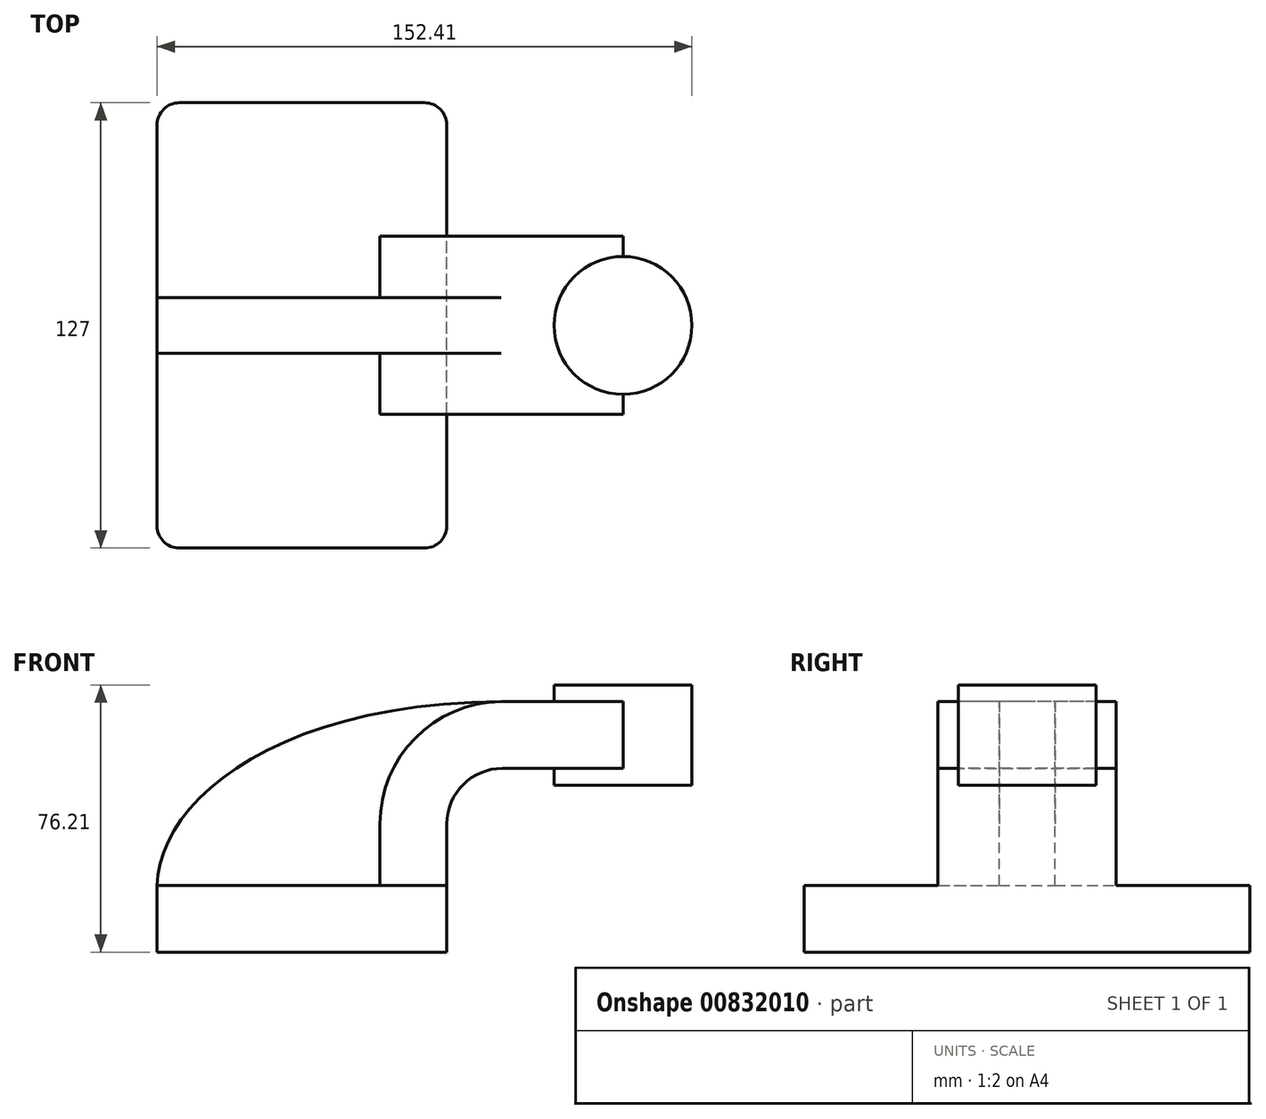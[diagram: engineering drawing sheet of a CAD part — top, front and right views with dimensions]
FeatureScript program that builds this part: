
annotation { "Feature Type Name" : "Feature", "Feature Type Description" : "" }
export const myFeature = defineFeature(function(context is Context, id is Id, definition is map)
    precondition{}
    {
        {
            var Q0;
            Q0=qCreatedBy(makeId("Front.planeOp"),FACE);
            var sketch = newSketch(context, id + "F0", { "sketchPlane" : qUnion([Q0])});
            skLineSegment(sketch, "E0.bottom", {"start": v(-41.28, 9.52) * mm, "end": v(41.27, 9.53) * mm});
            skLineSegment(sketch, "E0.top", {"start": v(-41.28, -9.52) * mm, "end": v(41.28, -9.52) * mm});
            skLineSegment(sketch, "E0.left", {"start": v(-41.28, 9.52) * mm, "end": v(-41.28, -9.53) * mm});
            skLineSegment(sketch, "E0.right", {"start": v(41.27, 9.53) * mm, "end": v(41.28, -9.52) * mm});
            skPoint(sketch, "E0.middle", {"position": v(0, 0) * mm});
            skLineSegment(sketch, "E1.bottom", {"start": v(111.13, 38.1) * mm, "end": v(60.32, 38.1) * mm});
            skLineSegment(sketch, "E1.top", {"start": v(111.12, 66.68) * mm, "end": v(60.32, 66.68) * mm});
            skLineSegment(sketch, "E1.left", {"start": v(111.12, 38.1) * mm, "end": v(111.12, 66.68) * mm});
            skLineSegment(sketch, "E1.right", {"start": v(60.32, 38.1) * mm, "end": v(60.32, 66.67) * mm});
            skPoint(sketch, "E1.middle", {"position": v(85.72, 52.39) * mm});
            skLineSegment(sketch, "E2", {"start": v(41.27, 9.53) * mm, "end": v(41.27, 27) * mm});
            skArc(sketch, "E3", {"start": v(41.27, 27) * mm, "mid": v(45.92, 38.23) * mm, "end": v(57.15, 42.88) * mm});
            skLineSegment(sketch, "E4", {"start": v(57.15, 42.88) * mm, "end": v(91.47, 42.88) * mm});
            skLineSegment(sketch, "E5.0", {"start": v(57.15, 61.93) * mm, "end": v(91.47, 61.93) * mm});
            skArc(sketch, "E5.1", {"start": v(22.22, 27) * mm, "mid": v(32.45, 51.7) * mm, "end": v(57.15, 61.93) * mm});
            skLineSegment(sketch, "E5.2", {"start": v(22.22, 9.53) * mm, "end": v(22.22, 27) * mm});
            skLineSegment(sketch, "E6", {"start": v(91.47, 61.93) * mm, "end": v(91.47, 42.88) * mm});
            skLineSegment(sketch, "E7", {"start": v(91.47, 42.88) * mm, "end": v(91.47, 38.1) * mm});
            skLineSegment(sketch, "E8", {"start": v(91.47, 38.1) * mm, "end": v(91.47, 61.93) * mm});
            skLineSegment(sketch, "E9", {"start": v(91.47, 66.68) * mm, "end": v(91.47, 61.93) * mm});
            skFitSpline(sketch, "E10", {"points": [v(-41.28, 9.52) * mm, v(57.15, 61.93) * mm], "startDerivative": vector(1.56, 69.77) * mm, "endDerivative": vector(197.26, 1.07) * mm});
            skSolve(sketch);
        }
        {
            var Q0;
            Q0=makeQuery(id+"F0.imprint","IMPRINT",FACE,{"disambiguationData":[TD([[makeQuery(id+"F0.imprint","IMPRINT",EDGE,{"derivedFrom":sQuery(id+"F0.wireOp",EDGE,"E0.top")}),1.0]])]});
            extrude(context, id + "F1", {"entities" : qUnion([Q0]), "endBound" : BoundingType.SYMMETRIC, "depth" : 127 * mm, "offsetDistance" : 25.4 * mm});
        }
        {
            var Q0;
            {var subQ1=sQuery(id+"F0.wireOp",EDGE,"E2");Q0=makeQuery(id+"F0.imprint","IMPRINT",FACE,{"disambiguationData":[TD([[makeQuery(id+"F0.imprint","IMPRINT",EDGE,{"derivedFrom":subQ1}),1.0]])]});}
            var Q1;
            {var subQ0=sQuery(id+"F0.wireOp",EDGE,"E4");var subQ1=sQuery(id+"F0.wireOp",EDGE,"E1.right");var subQ2=makeQuery(id+"F0.imprint","INTERSECT",VERTEX,{"derivedFrom":[subQ1,subQ0]});Q1=makeQuery(id+"F0.imprint","IMPRINT",FACE,{"disambiguationData":[TD([[makeQuery(id+"F0.imprint","IMPRINT",EDGE,{"disambiguationData":[TD([[subQ2,-1.0]])],"derivedFrom":subQ1}),-1.0]])]});}
            extrude(context, id + "F2", {"entities" : qUnion([Q0, Q1]), "operationType" : NewBodyOperationType.ADD, "endBound" : BoundingType.SYMMETRIC, "depth" : 50.8 * mm, "offsetDistance" : 25.4 * mm});
        }
        {
            var Q0;
            {var subQ3=sQuery(id+"F0.wireOp",EDGE,"E5.2");Q0=makeQuery(id+"F0.imprint","IMPRINT",FACE,{"disambiguationData":[TD([[makeQuery(id+"F0.imprint","IMPRINT",EDGE,{"derivedFrom":subQ3}),1.0]])]});}
            extrude(context, id + "F3", {"entities" : qUnion([Q0]), "operationType" : NewBodyOperationType.ADD, "endBound" : BoundingType.SYMMETRIC, "depth" : 15.88 * mm, "offsetDistance" : 25.4 * mm});
        }
        {
            var Q0;
            {var subQ0=sQuery(id+"F0.wireOp",EDGE,"E1.left");Q0=makeQuery(id+"F0.imprint","IMPRINT",FACE,{"disambiguationData":[TD([[makeQuery(id+"F0.imprint","IMPRINT",EDGE,{"derivedFrom":subQ0}),1.0]])]});}
            var Q1;
            Q1=sQuery(id+"F0.wireOp",EDGE,"E8");
            revolve(context, id + "F4", {"operationType" : NewBodyOperationType.ADD, "surfaceOperationType" : NewSurfaceOperationType.NEW, "entities" : qUnion([Q0]), "axis" : qUnion([Q1]), "revolveType" : RevolveType.FULL});
        }
        {
            var Q0;
            Q0=makeQuery(id+"F1.opExtrude","CAP_EDGE",EDGE,{"disambiguationData":[OSD([sQuery(id+"F0.wireOp",EDGE,"E0.right")])],"isStart":false});
            var Q1;
            Q1=makeQuery(id+"F1.opExtrude","CAP_EDGE",EDGE,{"disambiguationData":[OSD([sQuery(id+"F0.wireOp",EDGE,"E0.left")])],"isStart":false});
            var Q2;
            Q2=makeQuery(id+"F1.opExtrude","CAP_EDGE",EDGE,{"disambiguationData":[OSD([sQuery(id+"F0.wireOp",EDGE,"E0.right")])],"isStart":true});
            var Q3;
            Q3=makeQuery(id+"F1.opExtrude","CAP_EDGE",EDGE,{"disambiguationData":[OSD([sQuery(id+"F0.wireOp",EDGE,"E0.left")])],"isStart":true});
            fillet(context, id + "F5", {"entities" : qUnion([Q0, Q1, Q2, Q3]), "radius" : 6.35 * mm, "tangentPropagation" : true, "allowEdgeOverflow" : false});
        }
    });
